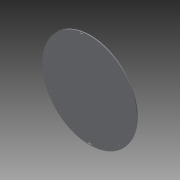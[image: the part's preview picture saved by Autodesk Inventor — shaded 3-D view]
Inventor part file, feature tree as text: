
AUTODESK INVENTOR PART (.ipt)
format: ipt  version: 2013 (Build 170138000, 138)  size: 110,592 bytes
history: native  units: in
note: dims shown in document units (in); Inventor stores cm internally (conversion verified against a paired STEP export)
features: extrude x1, sketch x1
ambient origin geometry x8: Origin, YZ Plane, XZ Plane, XY Plane, X Axis, Y Axis, Z Axis, Center Point
bodies: Solid1 (feature_tree)
feature tree (2):
  extrude  "Extrusion1"  Depth=0.25in
  sketch  "Sketch1"  dims[d0=28.0in d2=0.25in d3=6.6929in d5=360.0deg d7=0.5in d8=0.25in d9=1.0in d10=0.25in d11=0.0in]
